# Revit family: KingswayGroup_HtchSstms_ClinicRoomHatch
name_source: partatom
category: Generic Models
units: mm (PartAtom-declared; Revit-internal decimal feet)

## family parameters
Always vertical = No
Can host rebar = No
Cut with Voids When Loaded = No
Part Type = Normal
Room Calculation Point = No
Round Connector Dimension = Use Diameter
Shared = No
Work Plane-Based = No

## types (1)
- KingswayGroup_HtchSstms_ClinicRoomHatch
    AssetType = Fixed
    BIMObjectName = KingswayGroup_HatchSystems_ClinicRoomHatch
    Category = Ss_25_30_20_35:Hatch systems
    Color = For full range of available finishes and colours, contact Kingsway Group
    Default Elevation = 0 mm  [stored 0 ft]
    Description = Clinic Room Hatch For a 44mm Door
    DurationUnit = year
    Features = A secure Clinic Room Hatch unit that is installed into doors to provide a secure medicine serving solution. Manufactured to allow small items such as medicine to be passed through without the need to open the entire door leaf. It is flush to the patient side with no visible fixings and can be fitted with a folding serving shelf to the staff side.
    Finish = For full range of available finishes and colours, contact Kingsway Group
    HatchMaterial = NBS_Concept
    Manufacturer = Kingsway Group
    ManufacturerName = Kingsway Group
    ManufacturerURL = https://kingswaygroupglobal.com
    Material = For full range of available material, contact Kingsway Group
    Model = KG167
    ModelNumber = KG167
    ModelReference = Clinic Room Hatch
    Name = HatchSystems_ClinicRoomHatch_KG167_KingswayGroup
    NominalHeight = 846 mm  [stored 2.77559 ft]
    NominalLength = 584 mm  [stored 1.91601 ft]
    NominalWidth = 44 mm  [stored 0.144357 ft]
    PlateMaterial = NBS_Concept
    ProductInformation = https://kingswaygroupglobal.com
    Size = 584 x 846 x 44 mm
    URL = https://kingswaygroupglobal.com
    Uniclass2015Code = Ss_25_30_20_35
    Uniclass2015Title = Hatch systems
    Uniclass2015Version = Products v1.36
    Version = 1
    WarrantyDescription = 5-Year Guarantee *For faulty manufacture and not for damage
    WarrantyDurationParts = 5
    WarrantyDurationUnit = year

note: [stored X ft] marks values corroborated as IEEE doubles in the binary element streams (Revit-internal decimal feet)

## geometry (parser evidence)
native form markers: Sweep x2
no freeform markers — native parametric forms only
